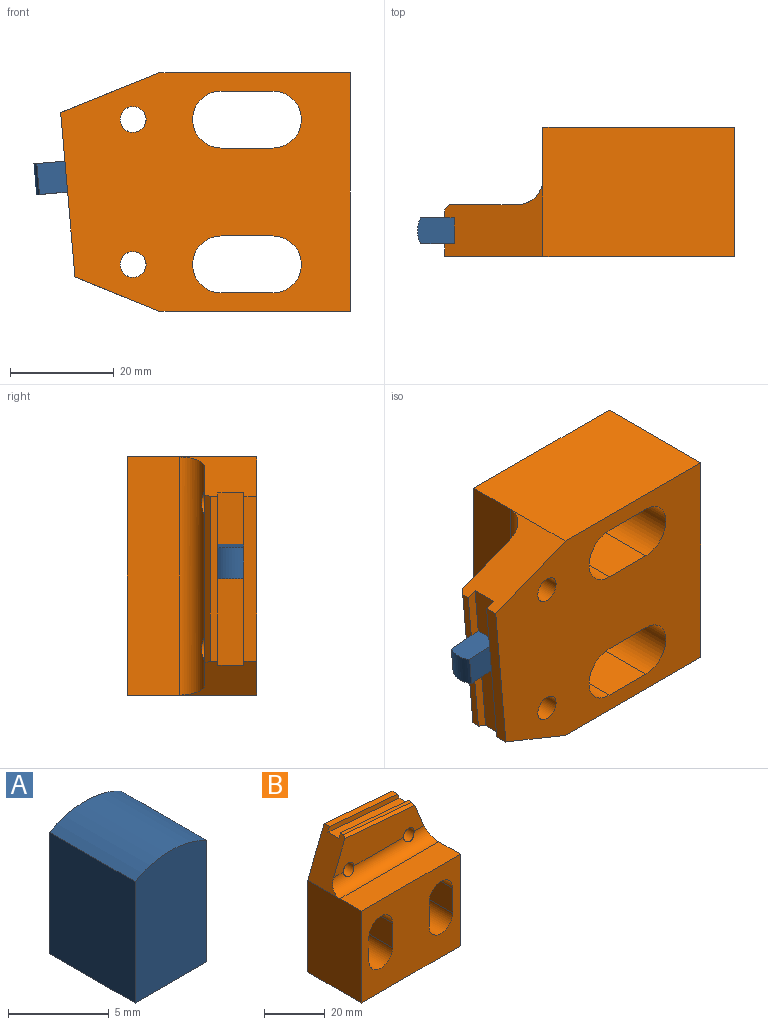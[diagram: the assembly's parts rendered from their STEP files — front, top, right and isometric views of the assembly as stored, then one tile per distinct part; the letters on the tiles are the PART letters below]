
ASSEMBLY  parts=2 mates=1
PART A: 6 faces, bbox 5x6x8 mm
  f0: cylinder r=5.2mm len=6mm, axis (0,1,0), area 31.3mm2, adj f1,f3,f4,f5
  f1: plane 7.36x6mm, normal (-1,0,0), area 44.2mm2, adj f0,f2,f4,f5
  f2: plane 6x5mm, normal (0,0,-1), area 30mm2, adj f1,f3,f4,f5
  f3: plane 7.36x6mm, normal (1,0,0), area 44.2mm2, adj f0,f2,f4,f5
  f4: plane 8x5mm, normal (0,-1,0), area 39mm2, adj f0,f1,f2,f3
  f5: plane 8x5mm, normal (0,1,0), area 39mm2, adj f0,f1,f2,f3
PART B: 26 faces, bbox 46x25x56 mm
  f0: plane 31.77x2.78mm, normal (0.09,0,1), area 79.7mm2, adj f1,f9,f20,f24
  f1: plane 56x46mm, normal (0,1,0), area 1938.2mm2, adj f0,f6,f7,f8,f9,f10,f11,f12
  f2: cylinder r=5mm len=46mm, axis (-1,0,0), area 329.4mm2, adj f3,f4,f9,f10,f11,f20
  f3: plane 41.96x13.03mm, normal (0,-1,0), area 413.7mm2, adj f2,f9,f10,f11,f20,f22
  f4: plane 46x10mm, normal (0,0,1), area 460mm2, adj f2,f5,f7,f8
  f5: plane 46x37mm, normal (0,-1,0), area 1291.9mm2, adj f4,f6,f7,f8,f12,f13,f14,f15
  f6: plane 46x25mm, normal (0,0,-1), area 1150mm2, adj f1,f5,f7,f8
  f7: plane 37x25mm, normal (1,0,0), area 925mm2, adj f1,f4,f5,f6,f20
  f8: plane 37x25mm, normal (-1,0,0), area 925mm2, adj f1,f4,f5,f6,f9
  f9: plane 19x15mm, normal (-0.93,0,0.37), area 200.2mm2, adj f0,f1,f2,f3,f8,f21,f22,f23
  f10: cylinder r=2.5mm len=10.67mm, axis (0,1,0), area 159.7mm2, adj f1,f2,f3
  f11: cylinder r=2.5mm len=10.67mm, axis (0,1,0), area 159.7mm2, adj f1,f2,f3
  f12: plane 25x10mm, normal (1,0,0), area 250mm2, adj f1,f5,f13,f15
  f13: cylinder r=5.5mm len=25mm, axis (0,1,0), area 432mm2, adj f1,f5,f12,f14
  f14: plane 25x10mm, normal (-1,0,0), area 250mm2, adj f1,f5,f13,f15
  f15: cylinder r=5.5mm len=25mm, axis (0,1,0), area 432mm2, adj f1,f5,f12,f14
  f16: plane 25x10mm, normal (1,0,0), area 250mm2, adj f1,f5,f17,f19
  f17: cylinder r=5.5mm len=25mm, axis (0,1,0), area 432mm2, adj f1,f5,f16,f18
  f18: plane 25x10mm, normal (-1,0,0), area 250mm2, adj f1,f5,f17,f19
  f19: cylinder r=5.5mm len=25mm, axis (0,1,0), area 432mm2, adj f1,f5,f16,f18
  f20: plane 16.22x15mm, normal (0.93,0,0.37), area 169.5mm2, adj f0,f1,f2,f3,f7,f21,f22,f23
  f21: plane 31.77x2.78mm, normal (0.09,0,1), area 47.8mm2, adj f9,f20,f22,f25
  f22: plane 32.58x3.82mm, normal (0.06,-0.71,0.7), area 45.7mm2, adj f3,f9,f20,f21
  f23: plane 33.32x5mm, normal (0.09,0,1), area 167.2mm2, adj f9,f20,f24,f25
  f24: plane 33.32x4.75mm, normal (0,-1,0), area 62.2mm2, adj f0,f9,f20,f23
  f25: plane 33.32x4.75mm, normal (0,1,0), area 62.2mm2, adj f9,f20,f21,f23
PLACE A rot(axis=(-0.59,-0.59,0.54),122.9deg) t=(-7.88,1.89,17.58)mm
PLACE B rot(axis=(0.71,0,-0.71),180deg) t=(41.13,-41.21,40.84)mm fixed
MATE fastened A.f2 <-> B.f23  axis (1,0,0.09) through (-3.39,-21.35,20.98)mm
